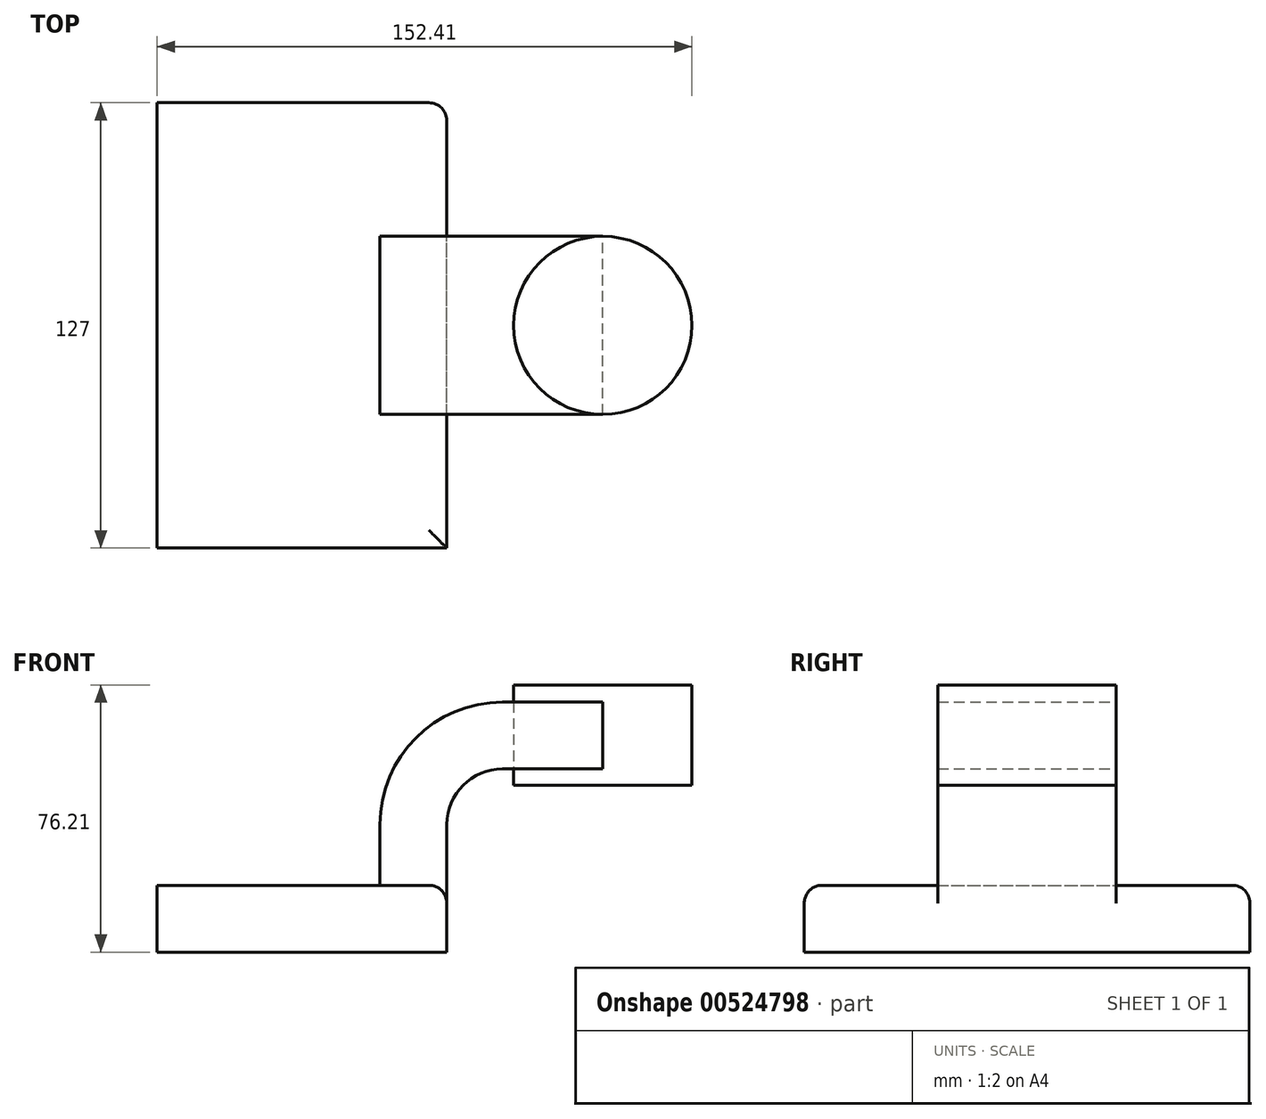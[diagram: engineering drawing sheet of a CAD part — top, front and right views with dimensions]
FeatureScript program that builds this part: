
annotation { "Feature Type Name" : "Feature", "Feature Type Description" : "" }
export const myFeature = defineFeature(function(context is Context, id is Id, definition is map)
    precondition{}
    {
        {
            var Q0;
            Q0=qCreatedBy(makeId("Front.planeOp"),FACE);
            var sketch = newSketch(context, id + "F0", { "sketchPlane" : qUnion([Q0])});
            skLineSegment(sketch, "E0.bottom", {"start": v(41.28, -9.52) * mm, "end": v(-41.28, -9.52) * mm});
            skLineSegment(sketch, "E0.top", {"start": v(41.27, 9.53) * mm, "end": v(-41.28, 9.53) * mm});
            skLineSegment(sketch, "E0.left", {"start": v(41.28, -9.52) * mm, "end": v(41.28, 9.53) * mm});
            skLineSegment(sketch, "E0.right", {"start": v(-41.28, -9.52) * mm, "end": v(-41.28, 9.53) * mm});
            skPoint(sketch, "E0.middle", {"position": v(0, 0) * mm});
            skLineSegment(sketch, "E1.bottom", {"start": v(60.33, 38.1) * mm, "end": v(111.12, 38.1) * mm});
            skLineSegment(sketch, "E1.top", {"start": v(60.33, 66.68) * mm, "end": v(111.12, 66.68) * mm});
            skLineSegment(sketch, "E1.left", {"start": v(60.33, 38.1) * mm, "end": v(60.33, 66.68) * mm});
            skLineSegment(sketch, "E1.right", {"start": v(111.12, 38.1) * mm, "end": v(111.12, 66.68) * mm});
            skPoint(sketch, "E1.middle", {"position": v(85.72, 52.39) * mm});
            skLineSegment(sketch, "E2", {"start": v(41.27, 9.53) * mm, "end": v(41.27, 26.83) * mm});
            skArc(sketch, "E3", {"start": v(41.27, 26.83) * mm, "mid": v(45.92, 38.06) * mm, "end": v(57.15, 42.7) * mm});
            skLineSegment(sketch, "E4", {"start": v(57.15, 42.7) * mm, "end": v(85.73, 42.7) * mm});
            skLineSegment(sketch, "E5.0", {"start": v(57.15, 61.76) * mm, "end": v(85.73, 61.76) * mm});
            skArc(sketch, "E5.1", {"start": v(22.22, 26.83) * mm, "mid": v(32.45, 51.53) * mm, "end": v(57.15, 61.76) * mm});
            skLineSegment(sketch, "E5.2", {"start": v(22.22, 9.53) * mm, "end": v(22.22, 26.83) * mm});
            skLineSegment(sketch, "E6", {"start": v(85.72, 38.1) * mm, "end": v(85.72, 66.68) * mm});
            skPoint(sketch, "E7.orphan", {"position": v(106.57, 42.7) * mm});
            skFitSpline(sketch, "E8", {"points": [v(-41.28, 9.53) * mm, v(57.15, 61.76) * mm], "startDerivative": vector(-0.29, 151.7) * mm, "endDerivative": vector(171.45, 0) * mm});
            skSolve(sketch);
        }
        {
            var Q0;
            Q0=makeQuery(id+"F0.imprint","IMPRINT",FACE,{"disambiguationData":[TD([[makeQuery(id+"F0.imprint","IMPRINT",EDGE,{"derivedFrom":sQuery(id+"F0.wireOp",EDGE,"E0.bottom")}),-1.0]])]});
            extrude(context, id + "F1", {"entities" : qUnion([Q0]), "endBound" : BoundingType.SYMMETRIC, "depth" : 127 * mm, "offsetDistance" : 25.4 * mm});
        }
        {
            var Q0;
            {var subQ1=sQuery(id+"F0.wireOp",EDGE,"E2");Q0=makeQuery(id+"F0.imprint","IMPRINT",FACE,{"disambiguationData":[TD([[makeQuery(id+"F0.imprint","IMPRINT",EDGE,{"derivedFrom":subQ1}),1.0]])]});}
            var Q1;
            {var subQ0=sQuery(id+"F0.wireOp",EDGE,"E4");var subQ1=sQuery(id+"F0.wireOp",EDGE,"E1.left");var subQ2=makeQuery(id+"F0.imprint","INTERSECT",VERTEX,{"derivedFrom":[subQ1,subQ0]});Q1=makeQuery(id+"F0.imprint","IMPRINT",FACE,{"disambiguationData":[TD([[makeQuery(id+"F0.imprint","IMPRINT",EDGE,{"disambiguationData":[TD([[subQ2,-1.0]])],"derivedFrom":subQ1}),-1.0]])]});}
            extrude(context, id + "F2", {"entities" : qUnion([Q0, Q1]), "operationType" : NewBodyOperationType.ADD, "endBound" : BoundingType.SYMMETRIC, "depth" : 50.8 * mm, "offsetDistance" : 25.4 * mm});
        }
        {
            var Q0;
            Q0=makeQuery(id+"F0.imprint","IMPRINT",FACE,{"disambiguationData":[TD([[makeQuery(id+"F0.imprint","IMPRINT",EDGE,{"derivedFrom":sQuery(id+"F0.wireOp",EDGE,"E5.1")}),1.0]])]});
            extrude(context, id + "F3", {"entities" : qUnion([Q0]), "operationType" : NewBodyOperationType.ADD, "endBound" : BoundingType.SYMMETRIC, "depth" : 16.56 * mm, "offsetDistance" : 25.4 * mm});
        }
        {
            var Q0;
            {var subQ0=sQuery(id+"F0.wireOp",EDGE,"E1.right");Q0=makeQuery(id+"F0.imprint","IMPRINT",FACE,{"disambiguationData":[TD([[makeQuery(id+"F0.imprint","IMPRINT",EDGE,{"derivedFrom":subQ0}),1.0]])]});}
            var Q1;
            Q1=sQuery(id+"F0.wireOp",EDGE,"E6");
            revolve(context, id + "F4", {"entities" : qUnion([Q0]), "axis" : qUnion([Q1]), "revolveType" : RevolveType.FULL});
        }
        {
            var Q0;
            Q0=makeQuery(id+"F1.opExtrude","CAP_EDGE",EDGE,{"disambiguationData":[OSD([sQuery(id+"F0.wireOp",EDGE,"E0.top")])],"isStart":false});
            var Q1;
            {var subQ0=sQuery(id+"F0.wireOp",EDGE,"E0.left");var subQ1=sQuery(id+"F0.wireOp",EDGE,"E2");var subQ2=sQuery(id+"F0.wireOp",EDGE,"E0.top");Q1=makeQuery(id+"F2.boolean.opBoolean","SPLIT",EDGE,{"disambiguationData":[TD([makeQuery(id+"F1.opExtrude","CAP_FACE",FACE,{"disambiguationData":[OSD([sQuery(id+"F0.wireOp",EDGE,"E0.bottom"),subQ2,subQ0,sQuery(id+"F0.wireOp",EDGE,"E0.right")])],"isStart":false})])],"derivedFrom":makeQuery(id+"F1.opExtrude","SWEPT_EDGE",EDGE,{"disambiguationData":[OSD([subQ2,subQ0,subQ1])]})});}
            var Q2;
            {var subQ0=sQuery(id+"F0.wireOp",EDGE,"E2");var subQ1=sQuery(id+"F0.wireOp",EDGE,"E0.top");var subQ2=sQuery(id+"F0.wireOp",EDGE,"E0.left");Q2=makeQuery(id+"F2.boolean.opBoolean","SPLIT",EDGE,{"disambiguationData":[TD([makeQuery(id+"F1.opExtrude","CAP_FACE",FACE,{"disambiguationData":[OSD([sQuery(id+"F0.wireOp",EDGE,"E0.bottom"),subQ1,subQ2,sQuery(id+"F0.wireOp",EDGE,"E0.right")])],"isStart":true})])],"derivedFrom":makeQuery(id+"F1.opExtrude","SWEPT_EDGE",EDGE,{"disambiguationData":[OSD([subQ1,subQ2,subQ0])]})});}
            var Q3;
            Q3=makeQuery(id+"F1.opExtrude","CAP_EDGE",EDGE,{"disambiguationData":[OSD([sQuery(id+"F0.wireOp",EDGE,"E0.left")])],"isStart":true});
            var Q4;
            Q4=makeQuery(id+"F1.opExtrude","CAP_EDGE",EDGE,{"disambiguationData":[OSD([sQuery(id+"F0.wireOp",EDGE,"E0.top")])],"isStart":true});
            fillet(context, id + "F5", {"entities" : qUnion([Q0, Q1, Q2, Q3, Q4]), "radius" : 5.08 * mm, "tangentPropagation" : true, "allowEdgeOverflow" : false});
        }
    });
